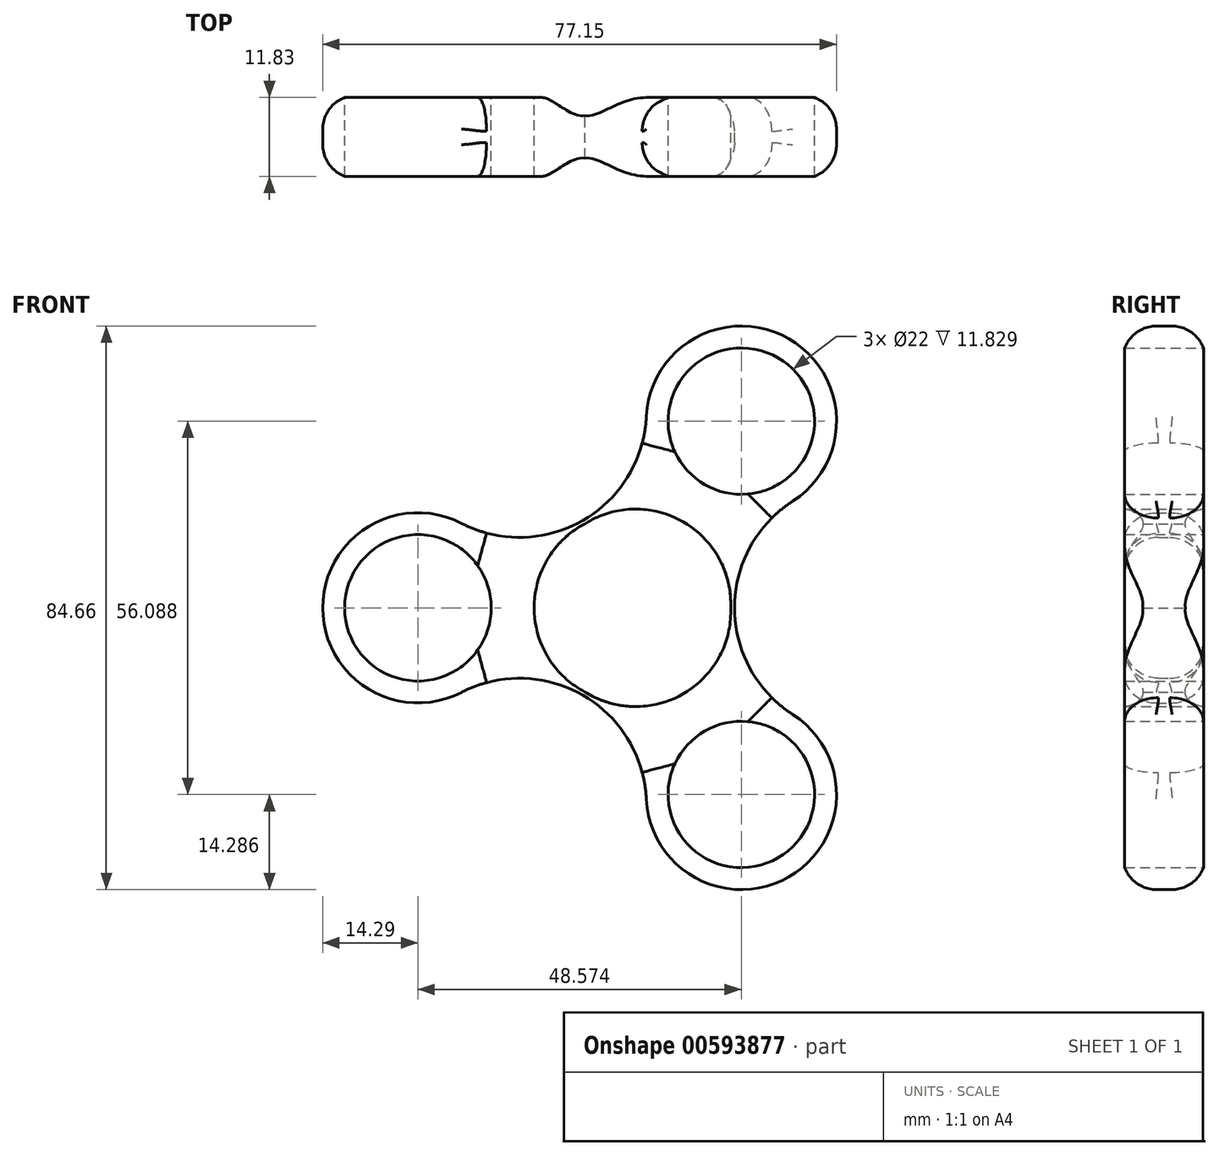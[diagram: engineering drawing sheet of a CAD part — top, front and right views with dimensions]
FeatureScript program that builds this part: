
annotation { "Feature Type Name" : "Feature", "Feature Type Description" : "" }
export const myFeature = defineFeature(function(context is Context, id is Id, definition is map)
    precondition{}
    {
        {
            var Q0;
            Q0=qCreatedBy(makeId("Front.planeOp"),FACE);
            var sketch = newSketch(context, id + "F0", { "sketchPlane" : qUnion([Q0])});
            skCircle(sketch, "E0", {"center": v(0, 0) * mm, "radius": 14.29 * mm});
            skCircle(sketch, "E1", {"center": v(0, 0) * mm, "radius": 11 * mm});
            skCircle(sketch, "E2", {"center": v(-31.75, 0) * mm, "radius": 14.29 * mm});
            skCircle(sketch, "E3", {"center": v(-31.75, 0) * mm, "radius": 11 * mm});
            skCircle(sketch, "E4.1.0", {"center": v(16.82, -28.04) * mm, "radius": 14.29 * mm});
            skCircle(sketch, "E4.1.1", {"center": v(16.82, -28.04) * mm, "radius": 11 * mm});
            skCircle(sketch, "E4.1.2", {"center": v(0.95, -0.55) * mm, "radius": 14.29 * mm});
            skCircle(sketch, "E4.1.3", {"center": v(0.95, -0.55) * mm, "radius": 11 * mm});
            skCircle(sketch, "E4.2.0", {"center": v(16.82, 28.04) * mm, "radius": 14.29 * mm});
            skCircle(sketch, "E4.2.1", {"center": v(16.82, 28.04) * mm, "radius": 11 * mm});
            skCircle(sketch, "E4.2.2", {"center": v(0.95, 0.55) * mm, "radius": 14.29 * mm});
            skCircle(sketch, "E4.2.3", {"center": v(0.95, 0.55) * mm, "radius": 11 * mm});
            skPoint(sketch, "E4.center", {"position": v(0.63, 0) * mm});
            skArc(sketch, "E5", {"start": v(24.55, 16.03) * mm, "mid": v(15.8, 0) * mm, "end": v(24.55, -16.03) * mm});
            skArc(sketch, "E6", {"start": v(-25.2, 12.7) * mm, "mid": v(-6.95, 13.13) * mm, "end": v(2.55, 28.72) * mm});
            skArc(sketch, "E7", {"start": v(2.55, -28.72) * mm, "mid": v(-6.95, -13.13) * mm, "end": v(-25.2, -12.7) * mm});
            skSolve(sketch);
        }
        {
            var Q0;
            Q0=qSketchRegion(id+"F0",true);
            var Q1;
            {var subQ6=sQuery(id+"F0.wireOp",EDGE,"E4.1.2");var subQ7=sQuery(id+"F0.wireOp",EDGE,"E0");var subQ8=makeQuery(id+"F0.imprint","INTERSECT",VERTEX,{"disambiguationData":[OD(0.0)],"derivedFrom":[subQ7,subQ6]});Q1=makeQuery(id+"F0.imprint","IMPRINT",FACE,{"disambiguationData":[TD([[makeQuery(id+"F0.imprint","IMPRINT",EDGE,{"disambiguationData":[TD([[subQ8,1.0]])],"derivedFrom":subQ7}),1.0]])]});}
            extrude(context, id + "F1", {"entities" : qUnion([Q0, Q1]), "depth" : 6.35 * mm, "offsetDistance" : 25.4 * mm});
        }
        {
            var Q0;
            Q0=makeQuery(id+"F1.opExtrude","SWEPT_BODY",BODY,{"disambiguationData":[OSD([sQuery(id+"F0.wireOp",EDGE,"E0"),sQuery(id+"F0.wireOp",EDGE,"E1"),sQuery(id+"F0.wireOp",EDGE,"E4.1.2"),sQuery(id+"F0.wireOp",EDGE,"E4.1.3"),sQuery(id+"F0.wireOp",EDGE,"E4.2.2"),sQuery(id+"F0.wireOp",EDGE,"E4.2.3")])]});
            deleteBodies(context, id + "F2", {"entities" : qUnion([Q0])});
        }
        {
            var Q0;
            Q0=makeQuery(id+"F1.opExtrude","CAP_FACE",FACE,{"disambiguationData":[OSD([sQuery(id+"F0.wireOp",EDGE,"E0"),sQuery(id+"F0.wireOp",EDGE,"E2"),sQuery(id+"F0.wireOp",EDGE,"E3"),sQuery(id+"F0.wireOp",EDGE,"E4.1.0"),sQuery(id+"F0.wireOp",EDGE,"E4.1.1"),sQuery(id+"F0.wireOp",EDGE,"E4.1.2"),sQuery(id+"F0.wireOp",EDGE,"E4.2.0"),sQuery(id+"F0.wireOp",EDGE,"E4.2.1"),sQuery(id+"F0.wireOp",EDGE,"E4.2.2"),sQuery(id+"F0.wireOp",EDGE,"E5"),sQuery(id+"F0.wireOp",EDGE,"E6"),sQuery(id+"F0.wireOp",EDGE,"E7")])],"isStart":true});
            var sketch = newSketch(context, id + "F3", { "sketchPlane" : qUnion([Q0])});
            skSolve(sketch);
        }
        {
            var Q0;
            Q0=makeQuery(id+"F3.imprint","IMPRINT",FACE,{"disambiguationData":[TD([[makeQuery(id+"F3.imprint","IMPRINT",EDGE,{"derivedFrom":makeQuery(id+"F1.opExtrude","CAP_EDGE",EDGE,{"disambiguationData":[OSD([sQuery(id+"F0.wireOp",EDGE,"E2")])],"isStart":true})}),-1.0]])]});
            extrude(context, id + "F4", {"entities" : qUnion([Q0]), "operationType" : NewBodyOperationType.ADD, "depth" : 5.48 * mm, "offsetDistance" : 25.4 * mm});
        }
        {
            var Q0;
            Q0=makeQuery(id+"F4.opExtrude","CAP_EDGE",EDGE,{"disambiguationData":[OSD([sQuery(id+"F0.wireOp",EDGE,"E5")])],"isStart":false});
            var Q1;
            Q1=makeQuery(id+"F4.opExtrude","CAP_EDGE",EDGE,{"disambiguationData":[OSD([sQuery(id+"F0.wireOp",EDGE,"E4.1.0")])],"isStart":false});
            var Q2;
            Q2=makeQuery(id+"F4.opExtrude","CAP_EDGE",EDGE,{"disambiguationData":[OSD([sQuery(id+"F0.wireOp",EDGE,"E7")])],"isStart":false});
            var Q3;
            Q3=makeQuery(id+"F4.opExtrude","CAP_EDGE",EDGE,{"disambiguationData":[OSD([sQuery(id+"F0.wireOp",EDGE,"E6")])],"isStart":false});
            var Q4;
            Q4=makeQuery(id+"F4.opExtrude","CAP_EDGE",EDGE,{"disambiguationData":[OSD([sQuery(id+"F0.wireOp",EDGE,"E2")])],"isStart":false});
            var Q5;
            Q5=makeQuery(id+"F4.opExtrude","CAP_EDGE",EDGE,{"disambiguationData":[OSD([sQuery(id+"F0.wireOp",EDGE,"E4.2.0")])],"isStart":false});
            fillet(context, id + "F5", {"entities" : qUnion([Q0, Q1, Q2, Q3, Q4, Q5]), "radius" : 5.08 * mm, "tangentPropagation" : true, "allowEdgeOverflow" : false});
        }
        {
            var Q0;
            Q0=makeQuery(id+"F1.opExtrude","CAP_EDGE",EDGE,{"disambiguationData":[OSD([sQuery(id+"F0.wireOp",EDGE,"E2")])],"isStart":false});
            var Q1;
            Q1=makeQuery(id+"F1.opExtrude","CAP_EDGE",EDGE,{"disambiguationData":[OSD([sQuery(id+"F0.wireOp",EDGE,"E4.2.0")])],"isStart":false});
            var Q2;
            Q2=makeQuery(id+"F1.opExtrude","CAP_EDGE",EDGE,{"disambiguationData":[OSD([sQuery(id+"F0.wireOp",EDGE,"E5")])],"isStart":false});
            var Q3;
            Q3=makeQuery(id+"F1.opExtrude","CAP_EDGE",EDGE,{"disambiguationData":[OSD([sQuery(id+"F0.wireOp",EDGE,"E4.1.0")])],"isStart":false});
            var Q4;
            Q4=makeQuery(id+"F1.opExtrude","CAP_EDGE",EDGE,{"disambiguationData":[OSD([sQuery(id+"F0.wireOp",EDGE,"E7")])],"isStart":false});
            var Q5;
            Q5=makeQuery(id+"F1.opExtrude","CAP_EDGE",EDGE,{"disambiguationData":[OSD([sQuery(id+"F0.wireOp",EDGE,"E6")])],"isStart":false});
            fillet(context, id + "F6", {"entities" : qUnion([Q0, Q1, Q2, Q3, Q4, Q5]), "radius" : 5.08 * mm, "tangentPropagation" : true, "allowEdgeOverflow" : false});
        }
    });
